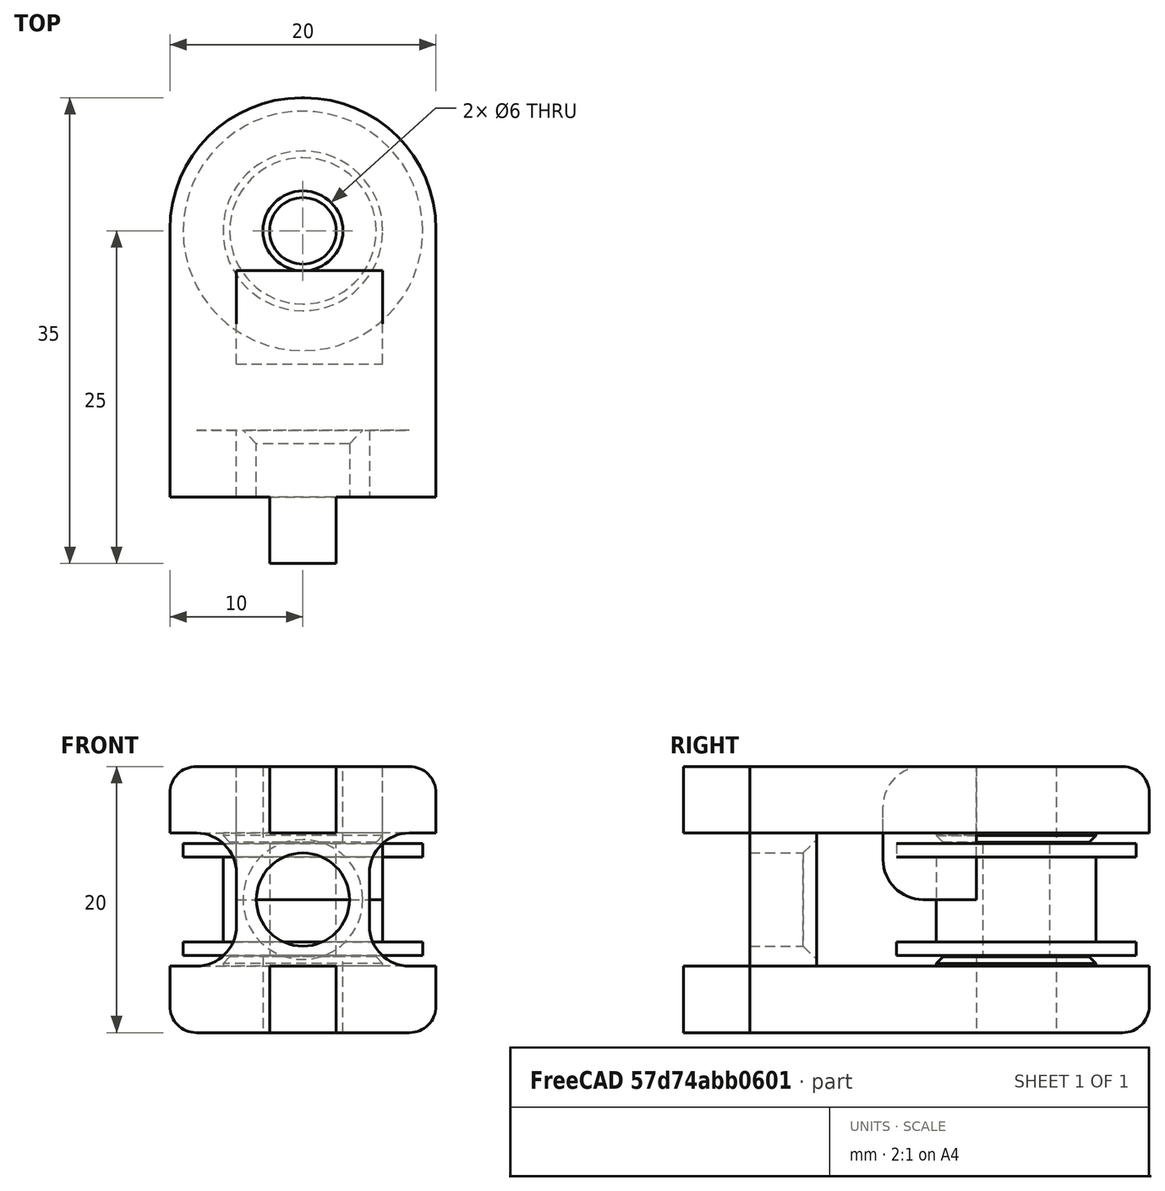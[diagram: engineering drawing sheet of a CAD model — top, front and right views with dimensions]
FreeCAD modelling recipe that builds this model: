
FCSTD DOCUMENT  (FreeCAD 0.20R29177 (Git))
Label: PoleaAcabados
License: All rights reserved
LicenseURL: http://en.wikipedia.org/wiki/All_rights_reserved
objects: Part::Cylinder×6, Part::Cut×4, Part::Box×4, Part::FeaturePython×3, Part::MultiFuse×3, Part::Refine×3, Part::Fillet×2, Part::Chamfer×2, Part::Fuse×1, Spreadsheet::Sheet×1, PartDesign::FeatureBase×1, PartDesign::Fillet×1, PartDesign::Body×1
note: 31 computed .brp shape members not serialized (recipe doc carries the construction recipe); baked Part::Feature solids carry a one-line shape summary decoded from their .brp

FEATURE [Part::Cylinder] Cylinder002  label="Cilindro002"
  Angle = 360
  AttacherType = Attacher::AttachEngine3D
  FirstAngle = 0
  Height = 1
  Placement = pos=(0,0,-4.2) rot=(0,0,1;0rad)
  Radius = 9
  SecondAngle = 0
FEATURE [Part::Cylinder] Cylinder003  label="Cilindro003"
  Angle = 360
  AttacherType = Attacher::AttachEngine3D
  FirstAngle = 0
  Height = 10
  Placement = pos=(0,0,-5) rot=(0,0,1;0rad)
  Radius = 2.5
  SecondAngle = 0
FEATURE [Part::Fuse] Fusion001
  Base = -> Cylinder002
FEATURE [Part::Cut] Cut  label="Pulley"
  Base = -> Fusion001
  Placement = pos=(0,15,0) rot=(0,0,1;0rad)
  Tool = -> Cylinder003
  expr: .Placement.Base.y = Spreadsheet.viajPolea
FEATURE [Spreadsheet::Sheet] Spreadsheet
  cells = A1=Nombre; B1=Valor; A2=viajPolea; B2(viajPolea)=15; A3=tol; B3(tol)=1; A4=esp; B4(esp)=5; A5=prof; B5(prof)=20; A6=profMedio; B6(profMedio)==B5 / 2; A7=espDob; B7(espDob)==B4 * 2; A8=espMedio; B8(espMedio)==B4 / 2; A9=profMedREsp; B9(profMedREsp)==B6 - B4; A10=lonPol; B10(lonPol)==B2 + B6
FEATURE [Part::Box] Box  label="Base"
  AttacherType = Attacher::AttachEngine3D
  Height = 20
  Length = 20
  Placement = pos=(-10,-5,-10) rot=(0,0,1;0rad)
  Width = 5
  expr: .Placement.Base.x = -Spreadsheet.profMedio
  expr: .Placement.Base.y = -Spreadsheet.esp
  expr: .Placement.Base.z = -Spreadsheet.profMedio
  expr: Height = Spreadsheet.prof
  expr: Length = Spreadsheet.prof
  expr: Width = Spreadsheet.esp
FEATURE [Part::Box] Box001  label="pin0"
  AttacherType = Attacher::AttachEngine3D
  Height = 5
  Length = 5
  Placement = pos=(-2.5,-10,5) rot=(0,0,1;0rad)
  Width = 10
  expr: .Placement.Base.x = -Spreadsheet.espMedio
  expr: .Placement.Base.y = -Spreadsheet.espDob
  expr: .Placement.Base.z = Spreadsheet.profMedREsp
  expr: Height = Spreadsheet.esp
  expr: Length = Spreadsheet.esp
  expr: Width = Spreadsheet.espDob
FEATURE [Part::FeaturePython] Clone  label="pin001"  # Draft clone (typed FeaturePython)
  AttacherType = Attacher::AttachEngine3D
  Fuse = false
  Objects = -> [Box001]
  Placement = pos=(-2.5,-10,-10) rot=(0,0,1;0rad)
  Scale = (1,1,1)
  expr: .Placement.Base.y = -Spreadsheet.espDob
  expr: .Placement.Base.z = -Spreadsheet.profMedio
FEATURE [Part::Box] Box002  label="pared1"
  AttacherType = Attacher::AttachEngine3D
  Height = 5
  Length = 20
  Placement = pos=(-10,0,5) rot=(0,0,1;0rad)
  Width = 25
  expr: .Placement.Base.x = -Spreadsheet.profMedio
  expr: .Placement.Base.z = Spreadsheet.profMedREsp
  expr: Height = Spreadsheet.esp
  expr: Length = Spreadsheet.prof
  expr: Width = Spreadsheet.lonPol
FEATURE [Part::FeaturePython] Clone001  label="pared002"  # Draft clone (typed FeaturePython)
  AttacherType = Attacher::AttachEngine3D
  Fuse = false
  Objects = -> [Box002]
  Placement = pos=(-10,0,-10) rot=(0,0,1;0rad)
  Scale = (1,1,1)
  expr: .Placement.Base.z = -Spreadsheet.profMedio
FEATURE [Part::MultiFuse] Fusion
  Shapes = -> [Box,Box001,Clone,Box002,Clone001]
FEATURE [Part::Refine] Fusion002
  Source = -> Fusion
FEATURE [Part::Cylinder] Cylinder004  label="Cilindro004"
  Angle = 360
  AttacherType = Attacher::AttachEngine3D
  FirstAngle = 0
  Height = 30
  Placement = pos=(0,15,-15) rot=(0,0,1;0rad)
  Radius = 3
  SecondAngle = 0
  expr: .Placement.Base.y = Spreadsheet.viajPolea
FEATURE [Part::Box] Box007  label="Cubo005"
  AttacherType = Attacher::AttachEngine3D
  Height = 10
  Length = 11
  Placement = pos=(10,5,-5) rot=(0,0,1;0rad)
  Width = 7
FEATURE [PartDesign::FeatureBase] BaseFeature
  BaseFeature = -> Box007
FEATURE [PartDesign::Fillet] Fillet
  Base = -> BaseFeature [Edge10,Edge9]
  BaseFeature = -> BaseFeature
  Radius = 3
  SupportTransform = false
  UseAllEdges = false
FEATURE [PartDesign::Body] Body
  BaseFeature = -> Box007
  Group = -> [BaseFeature,Fillet]
  Origin = -> Origin
  Placement = pos=(-5,5,0) rot=(0,0,1;0rad)
  Tip = -> Fillet
FEATURE [Part::FeaturePython] Array  # Draft array (typed FeaturePython)
  AlwaysSyncPlacement = false
  Angle = 180
  ArrayType = 1
  Axis = (0,0,1)
  Base = -> Body
  Center = (0,0,0)
  Count = 2
  ExpandArray = false
  Fuse = false
  IntervalAxis = (0,0,0)
  IntervalX = (50,0,0)
  IntervalY = (0,50,0)
  IntervalZ = (0,0,50)
  NumberCircles = 3
  NumberPolar = 2
  NumberX = 2
  NumberY = 2
  NumberZ = 1
  Placement = pos=(0,-3,-5) rot=(0,0,1;1.5708rad)
  PlacementList = 2 placements: [(-5,5,0),(5,-5,0)]
  RadialDistance = 50
  ScaleList = (2) [(1,1,1),(1,1,1)]
  Symmetry = 1
  TangentialDistance = 25
  expr: .Placement.Base.z = -Spreadsheet.esp
FEATURE [Part::Cylinder] Cylinder  label="Cilindro"
  Angle = 360
  AttacherType = Attacher::AttachEngine3D
  FirstAngle = 0
  Height = 15
  Placement = pos=(0,5,0) rot=(1,0,0;1.5708rad)
  Radius = 3.5
  SecondAngle = 0
FEATURE [Part::Cylinder] Cylinder005  label="apoyo2"
  Angle = 360
  AttacherType = Attacher::AttachEngine3D
  FirstAngle = 0
  Height = 4
  Placement = pos=(0,0,-8.3) rot=(0,0,1;0rad)
  Radius = 6
  SecondAngle = 0
FEATURE [Part::Cylinder] Cylinder006  label="apoyo1"
  Angle = 360
  AttacherType = Attacher::AttachEngine3D
  FirstAngle = 0
  Height = 4
  Placement = pos=(0,0,4.3) rot=(0,0,1;0rad)
  Radius = 6
  SecondAngle = 0
FEATURE [Part::MultiFuse] Fusion003
  Placement = pos=(0,15,0) rot=(0,0,1;0rad)
  Shapes = -> [Cylinder005,Cylinder006]
  expr: .Placement.Base.y = Spreadsheet.viajPolea
FEATURE [Part::MultiFuse] Fusion004
  Shapes = -> [Fusion002,Fusion003]
FEATURE [Part::Refine] Fusion004001
  Source = -> Fusion004
FEATURE [Part::Cut] Cut001
  Base = -> Fusion004001
  Tool = -> Cylinder
FEATURE [Part::Cut] Cut002
  Base = -> Cut001
  Tool = -> Cylinder004
FEATURE [Part::Cut] Cut003
  Base = -> Cut002
  Tool = -> Array
FEATURE [Part::Fillet] Fillet001
  Base = -> Cut003
  Edges = 4 edges r=9.9: [Edge41,Edge53,Edge70,Edge81]
FEATURE [Part::Fillet] Fillet002
  Base = -> Fillet001
  Edges = 2 edges r=2: [Edge1,Edge77]
FEATURE [Part::Chamfer] Chamfer
  Base = -> Fillet002
  Edges = 1 edges r=1: [Edge107]
FEATURE [Part::Chamfer] Chamfer001
  Base = -> Chamfer
  Edges = 2 edges r=0.5: [Edge141,Edge142]
FEATURE [Part::Refine] Chamfer001001
  Source = -> Chamfer001
